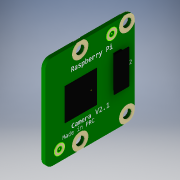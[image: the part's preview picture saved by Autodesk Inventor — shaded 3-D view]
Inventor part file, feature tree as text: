
AUTODESK INVENTOR PART (.ipt)
format: ipt  version: 2018 (Build 220112000, 112)  size: 2,342,400 bytes
history: native  units: mm
features: other x18, extrude x10, sketch x5, projected_geometry x5, hole x1, fillet x1
ambient origin geometry x8: Origin, YZ Plane, XZ Plane, XY Plane, X Axis, Y Axis, Z Axis, Center Point
bodies: Body1 (feature_tree), Body2 (feature_tree), Body3 (feature_tree), Body4 (feature_tree), Body5 (feature_tree), Body6 (feature_tree), Body7 (feature_tree), Body8 (feature_tree), Body9 (feature_tree)
feature tree (40):
  other  "PCB"
  sketch  "Boceto1"  dims[d0=23.862mm d1=25.0mm]
  extrude  "PCB_EXT"  Depth=25.0mm
  hole  "PADS_PCB_DRILL"  [1 undecoded]
  sketch  "Boceto2"  dims[d7=2.0mm d8=2.0mm]
  extrude  "PADS_PCB_DRILL_EXT"  Depth=1.0mm TaperAngle=0.0deg
  other  "FOTO"
  other  "SUPERIOR_PADS"
  extrude  "PADS_GOLDEN_UPPER_EXT"  Depth=2.2mm
  other  "INFERIOR_PADS"
  extrude  "PADS_GOLDEN_LOWER_EXT"  Depth=0.2mm
  extrude  "TEXTS_EXT"  Depth=0.2mm
  other  "REF_CON"
  extrude  "CONN"  Depth=0.2mm
  extrude  "CAM_BED"  Depth=0.2mm TaperAngle=0.0deg
  other  "PLANO_CON"
  extrude  "CONN_TOP"  Depth=0.2mm
  fillet  "Empalme2"  [1 undecoded]
  other  "REF_PADS_DRAW"
  extrude  "REF_PADS_DIAGONAL"  Depth=0.2mm TaperAngle=0.0deg
  extrude  "REF_PAD_BACK"  TaperAngle=90.0deg  [1 undecoded]
  other  "Imagen3"
  sketch  "Boceto4"  dims[d9=20.0mm d11=12.5mm d12=20.0mm d14=21.0mm d17=1.0mm d18=0.0mm]
  projected_geometry  "Contorno proyectado1"
  other  "PADS_UPPER"
  sketch  "Boceto5"  dims[d19=2.2mm d20=6.0mm d21=4.4mm d22=0.12mm d23=90.0deg d24=8.0mm d25=20.594885mm d26=2.0mm]
  projected_geometry  "Contorno proyectado2"
  projected_geometry  "Contorno proyectado3"
  projected_geometry  "Contorno proyectado4"
  projected_geometry  "Contorno proyectado5"
  other  "PADS_LOWER"
  other  "text_front"
  other  "TEXTS"
  other  "CAMERA_BED"
  sketch  "Boceto8"  dims[d27=4.4mm d28=4.4mm d29=4.4mm d30=4.4mm d31=0.13mm d32=0.0mm d57=24.8mm d63=90.0deg d66=0.07mm d67=0.0mm d68=90.0deg d69=0.07mm d70=0.0mm d71=0.03mm d72=0.0mm d74=8.5mm d75=8.5mm d78=5.212mm d79=8.25mm d82=4.7mm d86=2.2mm d87=8.5mm d88=0.5mm d89=1.0mm d90=0.0mm d91=0.1mm d92=0.0mm d93=90.0deg d94=0.1mm d95=0.0mm d97=0.2mm d98=13.8mm d101=0.1mm d102=0.0mm d115=0.1mm d116=0.0mm]
  other  "CONNECTOR"
  other  "PLACEMENT_CAM"
  other  "OUTSIDE_REF"
  other  "ref_pad_back_draw"
  other  "REF_PAD_BACK_PCB"
note: 3 required parameter values undecoded (feature->parameter linkage not recoverable at this tier; creation-order binding heuristic only, values carry confidence <= 0.55)
